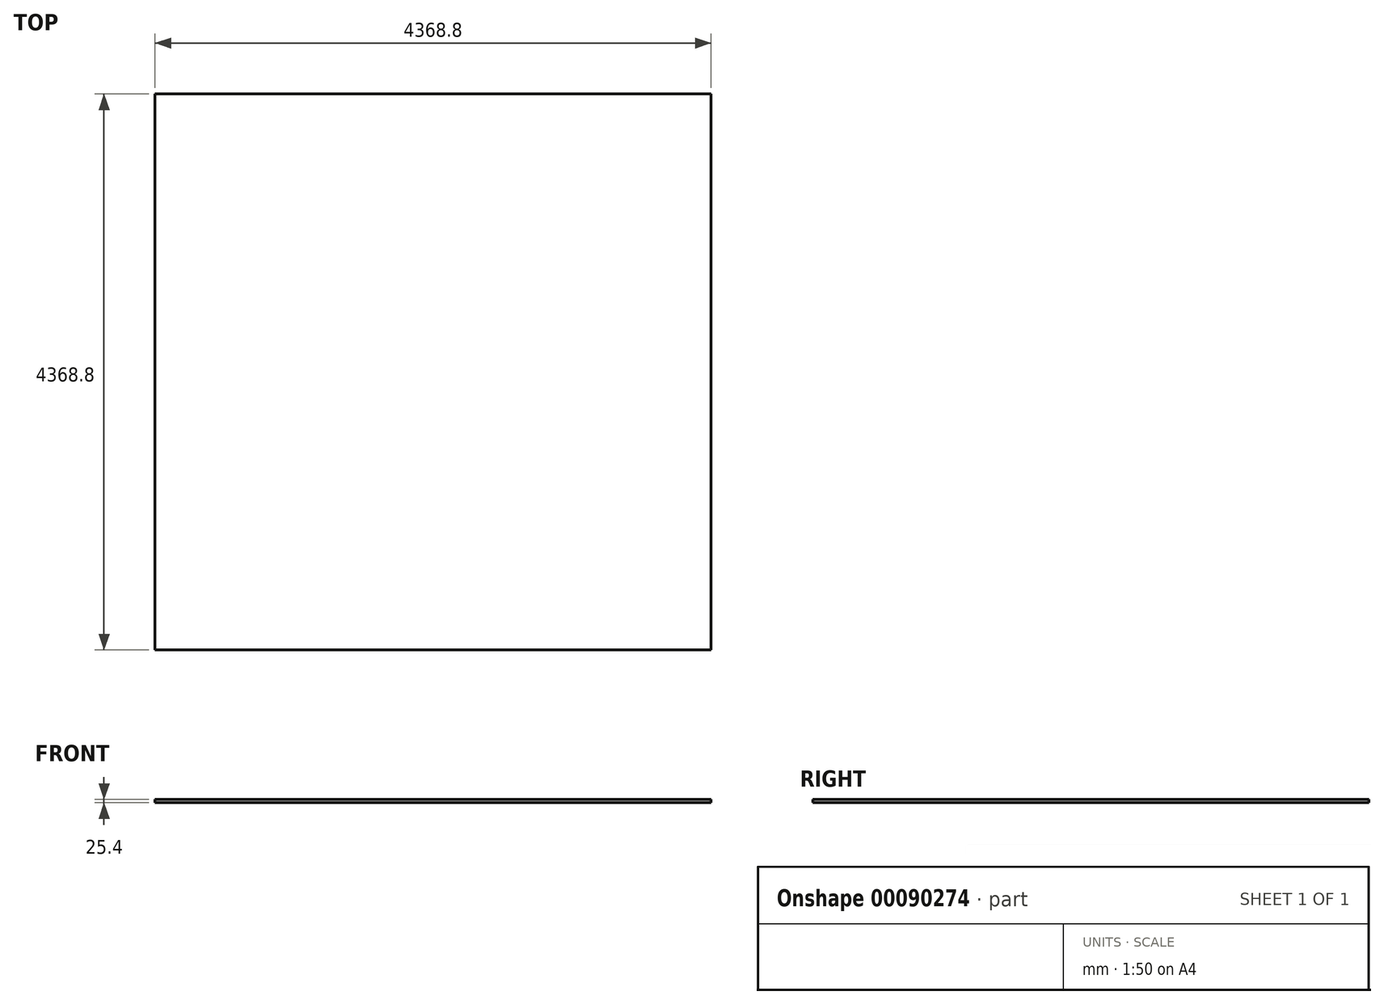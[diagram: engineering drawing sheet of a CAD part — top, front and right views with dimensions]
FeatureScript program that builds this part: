
annotation { "Feature Type Name" : "Feature", "Feature Type Description" : "" }
export const myFeature = defineFeature(function(context is Context, id is Id, definition is map)
    precondition{}
    {
        {
            var Q0;
            Q0=qCreatedBy(makeId("Top.planeOp"),FACE);
            var sketch = newSketch(context, id + "F0", { "sketchPlane" : qUnion([Q0])});
            skLineSegment(sketch, "E0.bottom", {"start": v(0, 0) * mm, "end": v(-4368.8, 0) * mm});
            skLineSegment(sketch, "E0.top", {"start": v(0, -4368.8) * mm, "end": v(-4368.8, -4368.8) * mm});
            skLineSegment(sketch, "E0.left", {"start": v(0, 0) * mm, "end": v(0, -4368.8) * mm});
            skLineSegment(sketch, "E0.right", {"start": v(-4368.8, 0) * mm, "end": v(-4368.8, -4368.8) * mm});
            skSolve(sketch);
        }
        {
            var Q0;
            Q0 = qSketchRegion(id + "F0", true);
            extrude(context, id + "F1", {"entities" : qUnion([Q0]), "depth" : 25.4 * mm});
        }
    });
